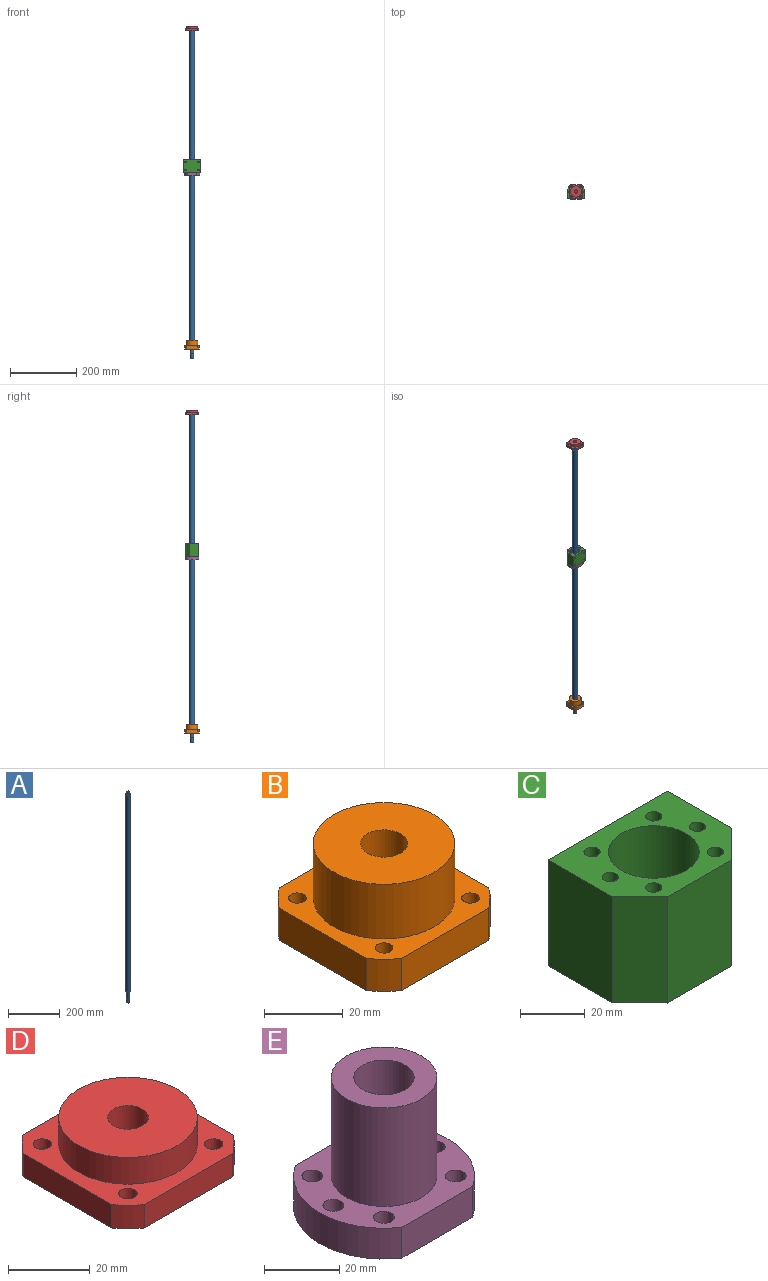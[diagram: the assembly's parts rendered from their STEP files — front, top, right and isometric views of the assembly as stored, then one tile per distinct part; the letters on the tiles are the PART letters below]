
ASSEMBLY  parts=5 mates=10
PART A: 9 faces, bbox 16x16x1000 mm
  f0: cylinder r=5mm len=11mm, axis (0,0,-1), area 345.6mm2, adj f1,f2
  f1: plane 10x10mm, normal (0,0,1), area 78.5mm2, adj f0
  f2: plane 16x16mm, normal (0,0,1), area 122.5mm2, adj f0,f4
  f3: plane 16x16mm, normal (0,0,-1), area 88mm2, adj f4,f5
  f4: cylinder r=8mm len=935mm, axis (0,0,-1), area 46998.2mm2, adj f2,f3
  f5: cylinder r=6mm len=39mm, axis (0,0,-1), area 1470.3mm2, adj f3,f6
  f6: plane 12x12mm, normal (0,0,-1), area 34.6mm2, adj f5,f8
  f7: plane 10x10mm, normal (0,0,-1), area 78.5mm2, adj f8
  f8: cylinder r=5mm len=15mm, axis (0,0,-1), area 471.2mm2, adj f6,f7
PART B: 25 faces, bbox 44x44x27 mm
  f0: cylinder r=4mm len=8mm, axis (0,0,-1), area 100.5mm2, adj f14,f22
  f1: cylinder r=4mm len=8mm, axis (0,0,-1), area 100.5mm2, adj f14,f20
  f2: cylinder r=4mm len=8mm, axis (0,0,-1), area 100.5mm2, adj f14,f18
  f3: cylinder r=4mm len=8mm, axis (0,0,-1), area 100.5mm2, adj f14,f16
  f4: plane 31.31x10mm, normal (1,0,0), area 313mm2, adj f5,f11,f13,f14
  f5: cylinder r=27mm len=10mm, axis (0,0,-1), area 90.2mm2, adj f4,f6,f13,f14
  f6: plane 31.31x10mm, normal (0,1,0), area 313mm2, adj f5,f7,f13,f14
  f7: cylinder r=27mm len=10mm, axis (0,0,-1), area 90.2mm2, adj f6,f8,f13,f14
  f8: plane 31.31x10mm, normal (-1,0,0), area 313mm2, adj f7,f9,f13,f14
  f9: cylinder r=27mm len=10mm, axis (0,0,-1), area 90.2mm2, adj f8,f10,f13,f14
  f10: plane 31.31x10mm, normal (0,-1,0), area 313mm2, adj f9,f11,f13,f14
  f11: cylinder r=27mm len=10mm, axis (0,0,-1), area 90.2mm2, adj f4,f10,f13,f14
  f12: cylinder r=6mm len=27mm, axis (0,0,-1), area 1017.9mm2, adj f14,f24
  f13: plane 44x44mm, normal (0,0,1), area 782.9mm2, adj f4,f5,f6,f7,f8,f9,f10,f11
  f14: plane 44x44mm, normal (0,0,-1), area 1550.3mm2, adj f0,f1,f2,f3,f4,f5,f6,f7
  f15: cylinder r=2.25mm len=6mm, axis (0,0,-1), area 84.8mm2, adj f13,f16
  f16: plane 8x8mm, normal (0,0,-1), area 34.4mm2, adj f3,f15
  f17: cylinder r=2.25mm len=6mm, axis (0,0,-1), area 84.8mm2, adj f13,f18
  f18: plane 8x8mm, normal (0,0,-1), area 34.4mm2, adj f2,f17
  f19: cylinder r=2.25mm len=6mm, axis (0,0,-1), area 84.8mm2, adj f13,f20
  f20: plane 8x8mm, normal (0,0,-1), area 34.4mm2, adj f1,f19
  f21: cylinder r=2.25mm len=6mm, axis (0,0,-1), area 84.8mm2, adj f13,f22
  f22: plane 8x8mm, normal (0,0,-1), area 34.4mm2, adj f0,f21
  f23: cylinder r=18mm len=36mm, axis (0,0,-1), area 1922.7mm2, adj f13,f24
  f24: plane 36x36mm, normal (0,0,1), area 904.8mm2, adj f12,f23
PART C: 23 faces, bbox 52x40x40 mm
  f0: plane 52x40mm, normal (0,1,0), area 2001.5mm2, adj f1,f11,f13,f14,f15,f17,f19,f21
  f1: plane 40x28mm, normal (-1,0,0), area 1120mm2, adj f0,f2,f13,f14
  f2: plane 40x12mm, normal (-0.71,-0.71,0), area 678.8mm2, adj f1,f3,f13,f14
  f3: plane 40x28mm, normal (0,-1,0), area 1120mm2, adj f2,f4,f13,f14
  f4: plane 40x12mm, normal (0.71,-0.71,0), area 678.8mm2, adj f3,f11,f13,f14
  f5: cylinder r=2.5mm len=40mm, axis (0,0,-1), area 628.3mm2, adj f13,f14
  f6: cylinder r=2.5mm len=40mm, axis (0,0,-1), area 628.3mm2, adj f13,f14
  f7: cylinder r=2.5mm len=40mm, axis (0,0,-1), area 628.3mm2, adj f13,f14
  f8: cylinder r=2.5mm len=40mm, axis (0,0,-1), area 628.3mm2, adj f13,f14
  f9: cylinder r=2.5mm len=40mm, axis (0,0,-1), area 628.3mm2, adj f13,f14
  f10: cylinder r=14mm len=40mm, axis (0,0,-1), area 3518.6mm2, adj f13,f14
  f11: plane 40x28mm, normal (1,0,0), area 1120mm2, adj f0,f4,f13,f14
  f12: cylinder r=2.5mm len=40mm, axis (0,0,-1), area 628.3mm2, adj f13,f14
  f13: plane 52x40mm, normal (0,0,1), area 1202.4mm2, adj f0,f1,f2,f3,f4,f5,f6,f7
  f14: plane 52x40mm, normal (0,0,-1), area 1202.4mm2, adj f0,f1,f2,f3,f4,f5,f6,f7
  f15: cylinder r=2.5mm len=15mm, axis (0,1,0), area 235.6mm2, adj f0,f16
  f16: plane 5x5mm, normal (0,1,0), area 19.6mm2, adj f15
  f17: cylinder r=2.5mm len=15mm, axis (0,1,0), area 235.6mm2, adj f0,f18
  f18: plane 5x5mm, normal (0,1,0), area 19.6mm2, adj f17
  f19: cylinder r=2.5mm len=15mm, axis (0,1,0), area 235.6mm2, adj f0,f20
  f20: plane 5x5mm, normal (0,1,0), area 19.6mm2, adj f19
  f21: cylinder r=2.5mm len=15mm, axis (0,1,0), area 235.6mm2, adj f0,f22
  f22: plane 5x5mm, normal (0,1,0), area 19.6mm2, adj f21
PART D: 25 faces, bbox 42x42x15 mm
  f0: cylinder r=4mm len=8mm, axis (0,0,-1), area 100.5mm2, adj f14,f22
  f1: cylinder r=4mm len=8mm, axis (0,0,-1), area 100.5mm2, adj f14,f20
  f2: cylinder r=4mm len=8mm, axis (0,0,-1), area 100.5mm2, adj f14,f18
  f3: cylinder r=4mm len=8mm, axis (0,0,-1), area 100.5mm2, adj f14,f16
  f4: plane 30.66x7mm, normal (1,0,0), area 214.6mm2, adj f5,f11,f13,f14
  f5: cylinder r=26mm len=7mm, axis (0,0,-1), area 56.4mm2, adj f4,f6,f13,f14
  f6: plane 30.66x7mm, normal (0,1,0), area 214.6mm2, adj f5,f7,f13,f14
  f7: cylinder r=26mm len=7mm, axis (0,0,-1), area 56.4mm2, adj f6,f8,f13,f14
  f8: plane 30.66x7mm, normal (-1,0,0), area 214.6mm2, adj f7,f9,f13,f14
  f9: cylinder r=26mm len=7mm, axis (0,0,-1), area 56.4mm2, adj f8,f10,f13,f14
  f10: plane 30.66x7mm, normal (0,-1,0), area 214.6mm2, adj f9,f11,f13,f14
  f11: cylinder r=26mm len=7mm, axis (0,0,-1), area 56.4mm2, adj f4,f10,f13,f14
  f12: cylinder r=5mm len=15mm, axis (0,0,-1), area 471.2mm2, adj f14,f24
  f13: plane 42x42mm, normal (0,0,1), area 734.8mm2, adj f4,f5,f6,f7,f8,f9,f10,f11
  f14: plane 42x42mm, normal (0,0,-1), area 1426.8mm2, adj f0,f1,f2,f3,f4,f5,f6,f7
  f15: cylinder r=2.25mm len=4.5mm, axis (0,0,-1), area 42.4mm2, adj f13,f16
  f16: plane 8x8mm, normal (0,0,-1), area 34.4mm2, adj f3,f15
  f17: cylinder r=2.25mm len=4.5mm, axis (0,0,-1), area 42.4mm2, adj f13,f18
  f18: plane 8x8mm, normal (0,0,-1), area 34.4mm2, adj f2,f17
  f19: cylinder r=2.25mm len=4.5mm, axis (0,0,-1), area 42.4mm2, adj f13,f20
  f20: plane 8x8mm, normal (0,0,-1), area 34.4mm2, adj f1,f19
  f21: cylinder r=2.25mm len=4.5mm, axis (0,0,-1), area 42.4mm2, adj f13,f22
  f22: plane 8x8mm, normal (0,0,-1), area 34.4mm2, adj f0,f21
  f23: cylinder r=17mm len=34mm, axis (0,0,-1), area 854.5mm2, adj f13,f24
  f24: plane 34x34mm, normal (0,0,1), area 829.4mm2, adj f12,f23
PART E: 15 faces, bbox 48x40x42 mm
  f0: plane 26.53x10mm, normal (0,1,0), area 265.3mm2, adj f1,f3,f11,f12
  f1: cylinder r=24mm len=40mm, axis (0,0,-1), area 472.9mm2, adj f0,f2,f11,f12
  f2: plane 26.53x10mm, normal (0,-1,0), area 265.3mm2, adj f1,f3,f11,f12
  f3: cylinder r=24mm len=40mm, axis (0,0,-1), area 472.9mm2, adj f0,f2,f11,f12
  f4: cylinder r=2.75mm len=10mm, axis (0,0,-1), area 172.8mm2, adj f11,f12
  f5: cylinder r=2.75mm len=10mm, axis (0,0,-1), area 172.8mm2, adj f11,f12
  f6: cylinder r=2.75mm len=10mm, axis (0,0,-1), area 172.8mm2, adj f11,f12
  f7: cylinder r=2.75mm len=10mm, axis (0,0,-1), area 172.8mm2, adj f11,f12
  f8: cylinder r=2.75mm len=10mm, axis (0,0,-1), area 172.8mm2, adj f11,f12
  f9: cylinder r=2.75mm len=10mm, axis (0,0,-1), area 172.8mm2, adj f11,f12
  f10: cylinder r=8mm len=42mm, axis (0,0,-1), area 2111.2mm2, adj f12,f14
  f11: plane 48x40mm, normal (0,0,1), area 907.2mm2, adj f0,f1,f2,f3,f4,f5,f6,f7
  f12: plane 48x40mm, normal (0,0,-1), area 1321.9mm2, adj f0,f1,f2,f3,f4,f5,f6,f7
  f13: cylinder r=14mm len=32mm, axis (0,0,-1), area 2814.9mm2, adj f11,f14
  f14: plane 28x28mm, normal (0,0,1), area 414.7mm2, adj f10,f13
PLACE A t=(-2.27,-0.45,932.5)mm
PLACE B t=(-15.4,-246.76,959.5)mm
PLACE C rot(axis=(1,0,0),180deg) t=(-120.9,55.75,1533)mm
PLACE D t=(-105.01,-247.6,1921.5)mm
PLACE E t=(-19.88,74.23,1483)mm
MATE parallel D.f10 <-> B.f10  axis (0,-1,0) through (-51.13,13.99,1925)mm
MATE planar C.f13 <-> E.f1  axis (0,0,-1) through (-51.13,33.07,1493)mm
MATE cylindrical E.f5 <-> C.f7  axis (0,0,-1) through (-64.57,48.42,1488)mm
MATE cylindrical D.f5 <-> A.f0  axis (0,0,-1) through (-51.13,34.99,1929)mm
MATE cylindrical C.f10 <-> E.f1  axis (0,0,1) through (-51.13,34.99,1493)mm
MATE planar D.f5 <-> A.f0  axis (0,0,-1) through (-51.13,34.99,1921.5)mm
MATE planar B.f5 <-> A.f0  axis (0,0,1) through (-51.13,34.99,986.5)mm
MATE cylindrical E.f1 <-> A.f0  axis (0,0,-1) through (-51.13,34.99,1504)mm
MATE cylindrical B.f5 <-> A.f0  axis (0,0,-1) through (-51.13,34.99,986.5)mm
MATE cylindrical E.f9 <-> C.f6  axis (0,0,-1) through (-37.7,48.42,1488)mm
